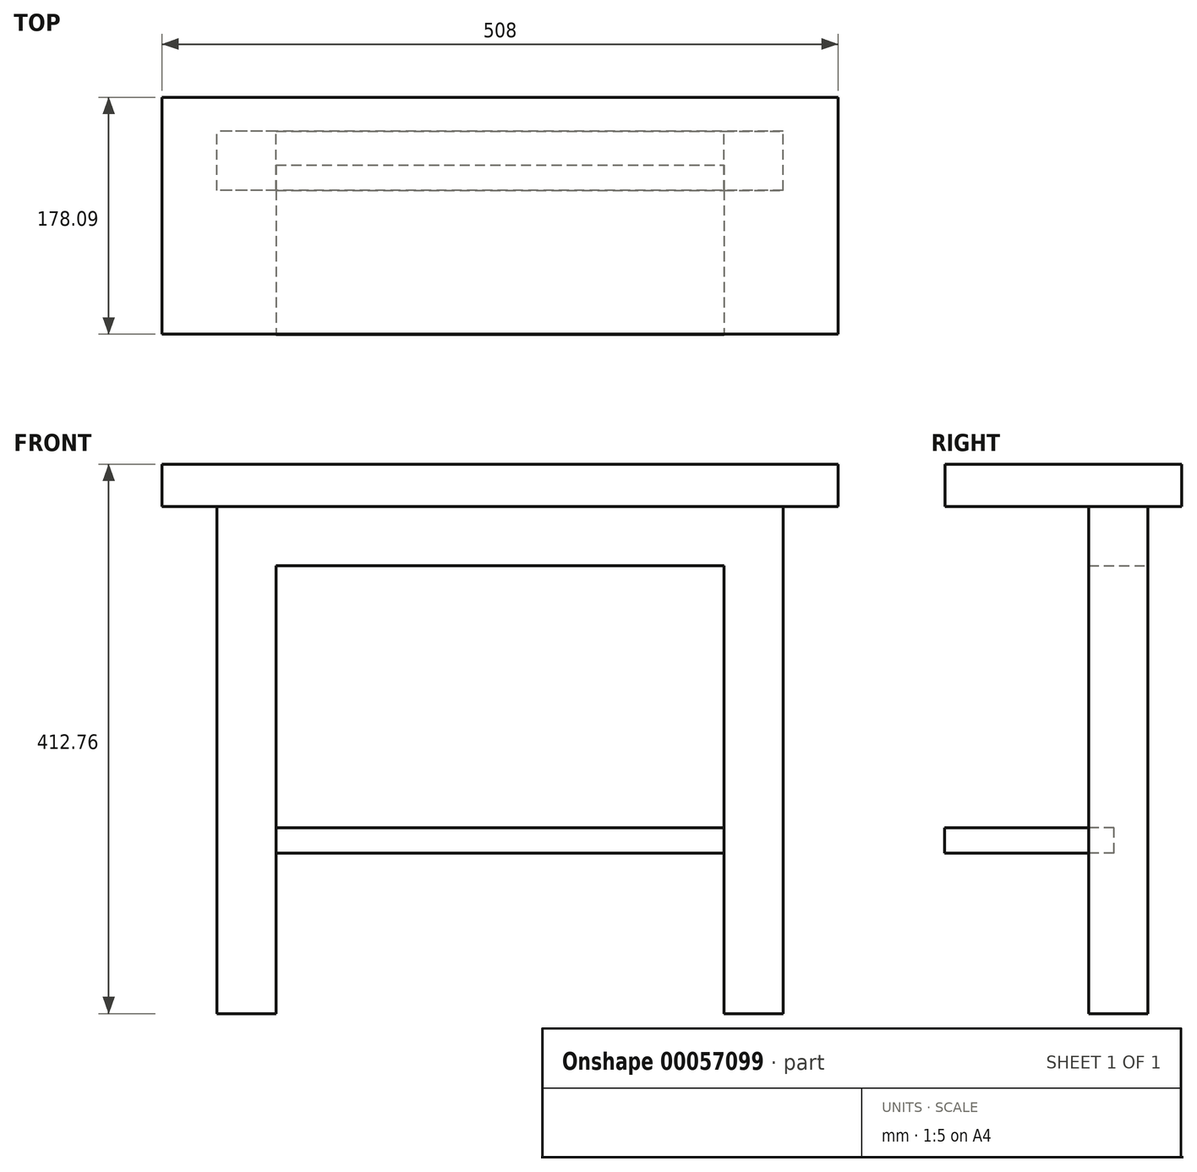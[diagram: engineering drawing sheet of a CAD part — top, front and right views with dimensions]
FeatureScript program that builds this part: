
annotation { "Feature Type Name" : "Feature", "Feature Type Description" : "" }
export const myFeature = defineFeature(function(context is Context, id is Id, definition is map)
    precondition{}
    {
        {
            var Q0;
            Q0=qCreatedBy(makeId("Front.planeOp"),FACE);
            var sketch = newSketch(context, id + "F0", { "sketchPlane" : qUnion([Q0])});
            skLineSegment(sketch, "E0.rect.bottom", {"start": v(-168.27, 22.23) * mm, "end": v(168.27, 22.23) * mm});
            skLineSegment(sketch, "E0.rect.top", {"start": v(-168.27, -22.23) * mm, "end": v(168.27, -22.23) * mm});
            skLineSegment(sketch, "E0.rect.left", {"start": v(-168.27, 22.23) * mm, "end": v(-168.27, -22.23) * mm});
            skLineSegment(sketch, "E0.rect.right", {"start": v(168.27, 22.22) * mm, "end": v(168.27, -22.23) * mm});
            skPoint(sketch, "E0.rect.middle", {"position": v(0, 0) * mm});
            skLineSegment(sketch, "E1.bottom", {"start": v(-168.27, 22.23) * mm, "end": v(-212.72, 22.22) * mm});
            skLineSegment(sketch, "E1.top", {"start": v(-168.27, -358.78) * mm, "end": v(-212.72, -358.78) * mm});
            skLineSegment(sketch, "E1.left", {"start": v(-168.28, 22.22) * mm, "end": v(-168.27, -358.78) * mm});
            skLineSegment(sketch, "E1.right", {"start": v(-212.72, 22.22) * mm, "end": v(-212.72, -358.78) * mm});
            skLineSegment(sketch, "E2.bottom", {"start": v(168.27, 22.22) * mm, "end": v(212.72, 22.23) * mm});
            skLineSegment(sketch, "E2.top", {"start": v(168.28, -358.78) * mm, "end": v(212.73, -358.78) * mm});
            skLineSegment(sketch, "E2.left", {"start": v(168.27, 22.22) * mm, "end": v(168.28, -358.78) * mm});
            skLineSegment(sketch, "E2.right", {"start": v(212.72, 22.22) * mm, "end": v(212.73, -358.78) * mm});
            skSolve(sketch);
        }
        {
            var Q0;
            Q0 = qSketchRegion(id + "F0", true);
            extrude(context, id + "F1", {"entities" : qUnion([Q0]), "depth" : 44.45 * mm});
        }
        {
            var Q0;
            Q0=makeQuery(id+"F1.opExtrude","SWEPT_FACE",FACE,{"disambiguationData":[OSD([sQuery(id+"F0.wireOp",EDGE,"E0.rect.bottom"),sQuery(id+"F0.wireOp",EDGE,"E1.bottom"),sQuery(id+"F0.wireOp",EDGE,"E2.bottom")])]});
            var sketch = newSketch(context, id + "F2", { "sketchPlane" : qUnion([Q0])});
            skLineSegment(sketch, "E3.bottom", {"start": v(-254, 25.4) * mm, "end": v(254, 25.4) * mm});
            skLineSegment(sketch, "E3.top", {"start": v(-254, -152.4) * mm, "end": v(254, -152.4) * mm});
            skLineSegment(sketch, "E3.left", {"start": v(-254, 25.4) * mm, "end": v(-254, -152.4) * mm});
            skLineSegment(sketch, "E3.right", {"start": v(254, 25.4) * mm, "end": v(254, -152.4) * mm});
            skSolve(sketch);
        }
        {
            var Q0;
            Q0 = qSketchRegion(id + "F2", true);
            extrude(context, id + "F3", {"entities" : qUnion([Q0]), "operationType" : NewBodyOperationType.ADD, "depth" : 31.75 * mm});
        }
        {
            var Q0;
            Q0=makeQuery(id+"F3.opExtrude","CAP_FACE",FACE,{"disambiguationData":[OSD([sQuery(id+"F2.wireOp",EDGE,"E3.bottom"),sQuery(id+"F2.wireOp",EDGE,"E3.top"),sQuery(id+"F2.wireOp",EDGE,"E3.left"),sQuery(id+"F2.wireOp",EDGE,"E3.right")])],"isStart":true});
            cPlane(context, id + "F4", {"entities" : qUnion([Q0]), "cplaneType" : CPlaneType.OFFSET, "offset" : 241.3 * mm, "width" : 152.4 * mm, "height" : 152.4 * mm});
        }
        {
            var Q0;
            Q0=qCreatedBy(id+"F4.planeOp",FACE);
            var sketch = newSketch(context, id + "F5", { "sketchPlane" : qUnion([Q0])});
            skLineSegment(sketch, "E4.bottom", {"start": v(-168.87, 25.4) * mm, "end": v(-168.27, 25.4) * mm});
            skLineSegment(sketch, "E5", {"start": v(-168.27, 25.4) * mm, "end": v(-168.27, 44.45) * mm});
            skLineSegment(sketch, "E6", {"start": v(168.28, 25.4) * mm, "end": v(168.28, 44.45) * mm});
            skLineSegment(sketch, "E7.bottom", {"start": v(-168.27, 25.4) * mm, "end": v(168.28, 25.4) * mm});
            skLineSegment(sketch, "E7.top", {"start": v(-168.27, 152.7) * mm, "end": v(168.28, 152.7) * mm});
            skLineSegment(sketch, "E7.left", {"start": v(-168.27, 25.4) * mm, "end": v(-168.27, 152.7) * mm});
            skLineSegment(sketch, "E7.right", {"start": v(168.28, 25.4) * mm, "end": v(168.28, 152.7) * mm});
            skSolve(sketch);
        }
        {
            var Q0;
            {var subQ0=sQuery(id+"F5.wireOp",EDGE,"E7.bottom");Q0=makeQuery(id+"F5.imprint","IMPRINT",FACE,{"disambiguationData":[TD([[makeQuery(id+"F5.imprint","IMPRINT",EDGE,{"derivedFrom":subQ0}),1.0]])]});}
            extrude(context, id + "F6", {"entities" : qUnion([Q0]), "operationType" : NewBodyOperationType.ADD, "depth" : 19.05 * mm});
        }
    });
